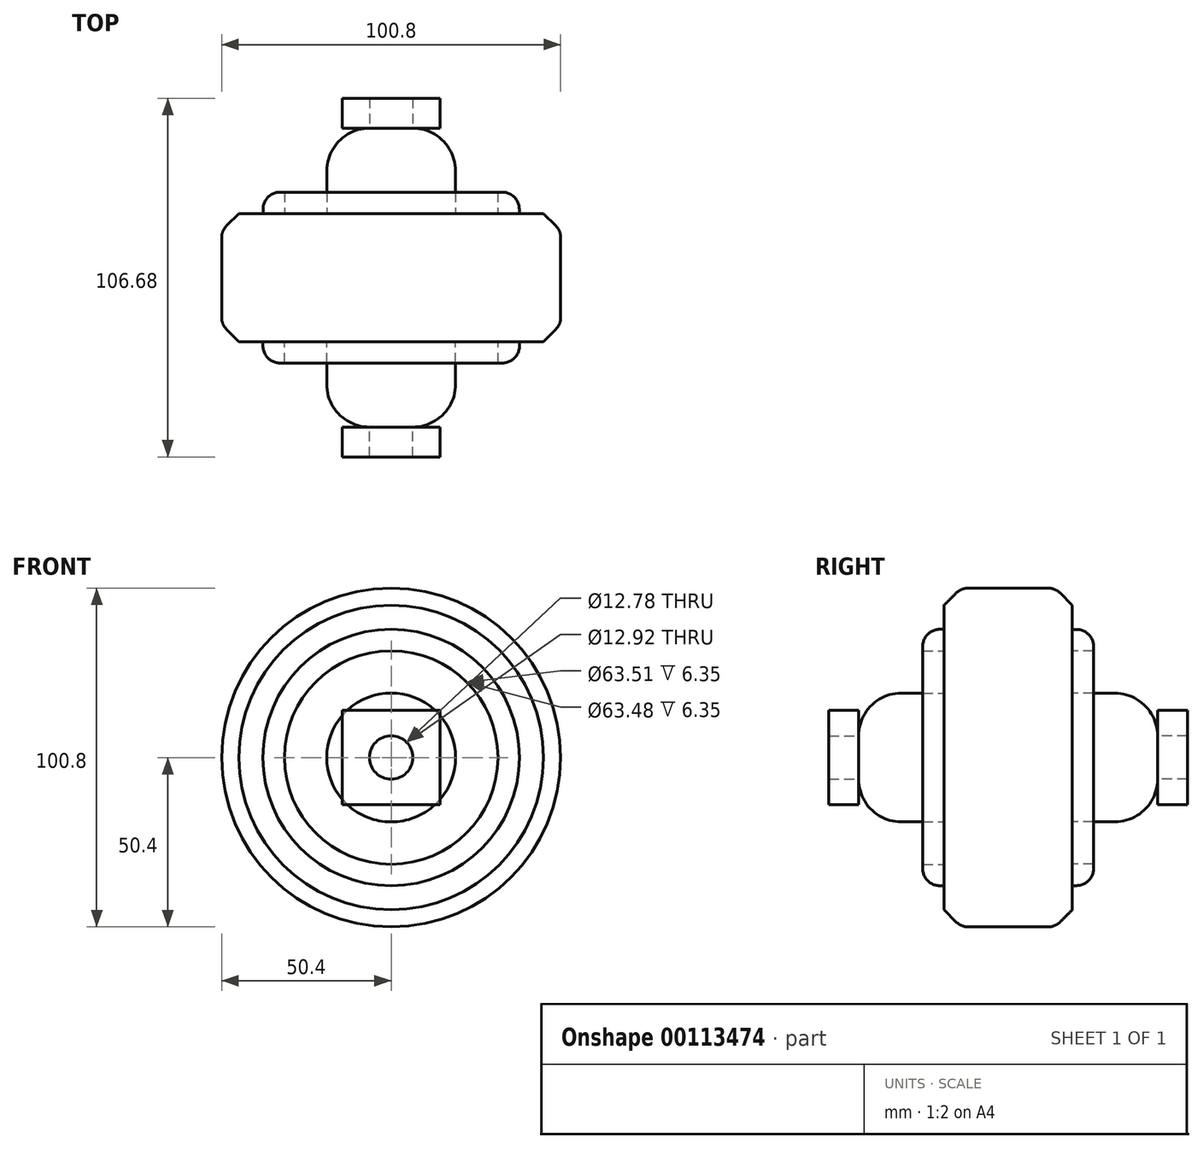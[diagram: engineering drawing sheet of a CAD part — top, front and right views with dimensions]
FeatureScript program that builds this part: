
annotation { "Feature Type Name" : "Feature", "Feature Type Description" : "" }
export const myFeature = defineFeature(function(context is Context, id is Id, definition is map)
    precondition{}
    {
        {
            var Q0;
            Q0=qCreatedBy(makeId("Front.planeOp"),FACE);
            var sketch = newSketch(context, id + "F0", { "sketchPlane" : qUnion([Q0])});
            skCircle(sketch, "E0", {"center": v(0, 0) * mm, "radius": 50.4 * mm});
            skSolve(sketch);
        }
        {
            var Q0;
            Q0=makeQuery(id+"F0.imprint","IMPRINT",FACE,{"disambiguationData":[TD([[makeQuery(id+"F0.imprint","IMPRINT",EDGE,{"derivedFrom":sQuery(id+"F0.wireOp",EDGE,"E0")}),1.0]])]});
            extrude(context, id + "F1", {"entities" : qUnion([Q0]), "depth" : 38.1 * mm});
        }
        {
            var Q0;
            Q0=makeQuery(id+"F1.opExtrude","CAP_EDGE",EDGE,{"disambiguationData":[OSD([sQuery(id+"F0.wireOp",EDGE,"E0")])],"isStart":false});
            chamfer(context, id + "F2", {"entities" : qUnion([Q0]), "width" : 5.08 * mm, "tangentPropagation" : true});
        }
        {
            var Q0;
            Q0=makeQuery(id+"F1.opExtrude","CAP_EDGE",EDGE,{"disambiguationData":[OSD([sQuery(id+"F0.wireOp",EDGE,"E0")])],"isStart":true});
            chamfer(context, id + "F3", {"entities" : qUnion([Q0]), "width" : 5.08 * mm, "tangentPropagation" : true});
        }
        {
            var Q0;
            Q0=makeQuery(id+"F1.opExtrude","CAP_FACE",FACE,{"disambiguationData":[OSD([sQuery(id+"F0.wireOp",EDGE,"E0")])],"isStart":false});
            var sketch = newSketch(context, id + "F4", { "sketchPlane" : qUnion([Q0])});
            skCircle(sketch, "E1", {"center": v(0, 0) * mm, "radius": 19.16 * mm});
            skSolve(sketch);
        }
        {
            var Q0;
            Q0=makeQuery(id+"F4.imprint","IMPRINT",FACE,{"disambiguationData":[TD([[makeQuery(id+"F4.imprint","IMPRINT",EDGE,{"derivedFrom":sQuery(id+"F4.wireOp",EDGE,"E1")}),1.0]])]});
            extrude(context, id + "F5", {"entities" : qUnion([Q0]), "operationType" : NewBodyOperationType.ADD, "depth" : 25.4 * mm});
        }
        {
            var Q0;
            Q0=makeQuery(id+"F1.opExtrude","CAP_FACE",FACE,{"disambiguationData":[OSD([sQuery(id+"F0.wireOp",EDGE,"E0")])],"isStart":true});
            var sketch = newSketch(context, id + "F6", { "sketchPlane" : qUnion([Q0])});
            skCircle(sketch, "E2", {"center": v(0, 0) * mm, "radius": 19.1 * mm});
            skSolve(sketch);
        }
        {
            var Q0;
            Q0=makeQuery(id+"F6.imprint","IMPRINT",FACE,{"disambiguationData":[TD([[makeQuery(id+"F6.imprint","IMPRINT",EDGE,{"derivedFrom":sQuery(id+"F6.wireOp",EDGE,"E2")}),1.0]])]});
            extrude(context, id + "F7", {"entities" : qUnion([Q0]), "operationType" : NewBodyOperationType.ADD, "depth" : 25.4 * mm});
        }
        {
            var Q0;
            Q0=makeQuery(id+"F7.opExtrude","CAP_EDGE",EDGE,{"disambiguationData":[OSD([sQuery(id+"F6.wireOp",EDGE,"E2")])],"isStart":false});
            fillet(context, id + "F8", {"entities" : qUnion([Q0]), "radius" : 12.7 * mm, "tangentPropagation" : true, "allowEdgeOverflow" : false});
        }
        {
            var Q0;
            Q0=makeQuery(id+"F5.opExtrude","CAP_EDGE",EDGE,{"disambiguationData":[OSD([sQuery(id+"F4.wireOp",EDGE,"E1")])],"isStart":false});
            fillet(context, id + "F9", {"entities" : qUnion([Q0]), "radius" : 12.7 * mm, "tangentPropagation" : true, "allowEdgeOverflow" : false});
        }
        {
            var Q0;
            Q0=makeQuery(id+"F5.opExtrude","CAP_FACE",FACE,{"disambiguationData":[OSD([sQuery(id+"F4.wireOp",EDGE,"E1")])],"isStart":false});
            var sketch = newSketch(context, id + "F10", { "sketchPlane" : qUnion([Q0])});
            skLineSegment(sketch, "E3.bottom", {"start": v(-14.5, -14.09) * mm, "end": v(14.5, -14.09) * mm});
            skLineSegment(sketch, "E3.top", {"start": v(-14.5, 14.09) * mm, "end": v(14.5, 14.09) * mm});
            skLineSegment(sketch, "E3.left", {"start": v(-14.5, -14.09) * mm, "end": v(-14.5, 14.09) * mm});
            skLineSegment(sketch, "E3.right", {"start": v(14.5, -14.09) * mm, "end": v(14.5, 14.09) * mm});
            skPoint(sketch, "E3.middle", {"position": v(0, 0) * mm});
            skSolve(sketch);
        }
        {
            var Q0;
            Q0=makeQuery(id+"F10.imprint","IMPRINT",FACE,{"disambiguationData":[TD([[makeQuery(id+"F10.imprint","IMPRINT",EDGE,{"derivedFrom":sQuery(id+"F10.wireOp",EDGE,"E3.bottom")}),1.0]])]});
            extrude(context, id + "F11", {"entities" : qUnion([Q0]), "depth" : 8.9 * mm});
        }
        {
            var Q0;
            Q0=makeQuery(id+"F7.opExtrude","CAP_FACE",FACE,{"disambiguationData":[OSD([sQuery(id+"F6.wireOp",EDGE,"E2")])],"isStart":false});
            var sketch = newSketch(context, id + "F12", { "sketchPlane" : qUnion([Q0])});
            skLineSegment(sketch, "E4.bottom", {"start": v(-14.5, -14.09) * mm, "end": v(14.5, -14.09) * mm});
            skLineSegment(sketch, "E4.top", {"start": v(-14.5, 14.09) * mm, "end": v(14.5, 14.09) * mm});
            skLineSegment(sketch, "E4.left", {"start": v(-14.5, -14.09) * mm, "end": v(-14.5, 14.09) * mm});
            skLineSegment(sketch, "E4.right", {"start": v(14.5, -14.09) * mm, "end": v(14.5, 14.09) * mm});
            skPoint(sketch, "E4.middle", {"position": v(0, 0) * mm});
            skSolve(sketch);
        }
        {
            var Q0;
            Q0=makeQuery(id+"F12.imprint","IMPRINT",FACE,{"disambiguationData":[TD([[makeQuery(id+"F12.imprint","IMPRINT",EDGE,{"derivedFrom":sQuery(id+"F12.wireOp",EDGE,"E4.bottom")}),1.0]])]});
            extrude(context, id + "F13", {"entities" : qUnion([Q0]), "depth" : 8.9 * mm});
        }
        {
            var Q0;
            Q0=makeQuery(id+"F1.opExtrude","CAP_FACE",FACE,{"disambiguationData":[OSD([sQuery(id+"F0.wireOp",EDGE,"E0")])],"isStart":false});
            var sketch = newSketch(context, id + "F14", { "sketchPlane" : qUnion([Q0])});
            skCircle(sketch, "E5", {"center": v(0, 0) * mm, "radius": 31.75 * mm});
            skCircle(sketch, "E6", {"center": v(0, 0) * mm, "radius": 38.14 * mm});
            skSolve(sketch);
        }
        {
            var Q0;
            Q0=makeQuery(id+"F14.imprint","IMPRINT",FACE,{"disambiguationData":[TD([[makeQuery(id+"F14.imprint","IMPRINT",EDGE,{"derivedFrom":sQuery(id+"F14.wireOp",EDGE,"E5")}),-1.0]])]});
            extrude(context, id + "F15", {"entities" : qUnion([Q0]), "operationType" : NewBodyOperationType.ADD, "depth" : 6.35 * mm});
        }
        {
            var Q0;
            Q0=makeQuery(id+"F1.opExtrude","CAP_FACE",FACE,{"disambiguationData":[OSD([sQuery(id+"F0.wireOp",EDGE,"E0")])],"isStart":true});
            var sketch = newSketch(context, id + "F16", { "sketchPlane" : qUnion([Q0])});
            skCircle(sketch, "E7", {"center": v(0, 0) * mm, "radius": 31.74 * mm});
            skCircle(sketch, "E8", {"center": v(0, 0) * mm, "radius": 38.1 * mm});
            skSolve(sketch);
        }
        {
            var Q0;
            Q0=makeQuery(id+"F16.imprint","IMPRINT",FACE,{"disambiguationData":[TD([[makeQuery(id+"F16.imprint","IMPRINT",EDGE,{"derivedFrom":sQuery(id+"F16.wireOp",EDGE,"E7")}),-1.0]])]});
            extrude(context, id + "F17", {"entities" : qUnion([Q0]), "operationType" : NewBodyOperationType.ADD, "depth" : 6.35 * mm});
        }
        {
            var Q0;
            Q0=makeQuery(id+"F15.opExtrude","CAP_EDGE",EDGE,{"disambiguationData":[OSD([sQuery(id+"F14.wireOp",EDGE,"E6")])],"isStart":false});
            fillet(context, id + "F18", {"entities" : qUnion([Q0]), "radius" : 5.08 * mm, "tangentPropagation" : true, "allowEdgeOverflow" : false});
        }
        {
            var Q0;
            Q0=makeQuery(id+"F17.opExtrude","CAP_EDGE",EDGE,{"disambiguationData":[OSD([sQuery(id+"F16.wireOp",EDGE,"E8")])],"isStart":false});
            fillet(context, id + "F19", {"entities" : qUnion([Q0]), "radius" : 5.08 * mm, "tangentPropagation" : true, "allowEdgeOverflow" : false});
        }
        {
            var Q0;
            Q0=makeQuery(id+"F1.opExtrude","SWEPT_FACE",FACE,{"disambiguationData":[OSD([sQuery(id+"F0.wireOp",EDGE,"E0")])]});
            fillet(context, id + "F20", {"entities" : qUnion([Q0]), "radius" : 5.08 * mm, "tangentPropagation" : true, "allowEdgeOverflow" : false});
        }
    });
